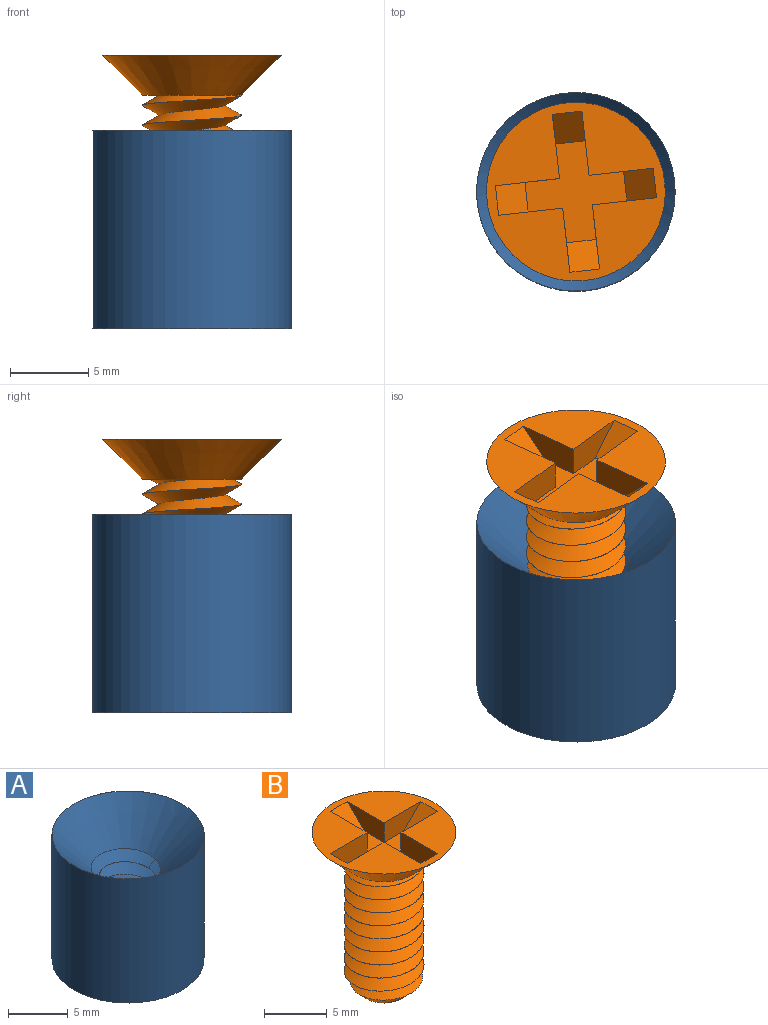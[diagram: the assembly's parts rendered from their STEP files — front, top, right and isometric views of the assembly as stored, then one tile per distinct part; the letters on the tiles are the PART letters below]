
ASSEMBLY  parts=2 mates=1
PART A: 9 faces, bbox 12.7x12.7x13.3 mm
  f0: plane 12.7x12.7mm, normal (0,0,-1), area 99.3mm2, adj f2,f5,f6
  f1: cylinder r=2.39mm len=8.74mm, axis (0,0,-1), area -8.6mm2, adj f5,f6,f8
  f2: cylinder r=6.35mm len=12.7mm, axis (0,0,-1), area 506.7mm2, adj f0,f3
  f3: plane 12.7x12.7mm, normal (0,0,1), area 0.1mm2, adj f2,f4
  f4: cone r=2.39mm half-angle=45deg, axis (0,0,1), area 140.3mm2, adj f3,f6,f7,f8
  f5: bspline ~9.37x6.97mm, area 155.6mm2, adj f0,f1,f6,f8
  f6: bspline ~10.01x6.97mm, area 166mm2, adj f0,f1,f4,f5,f7,f8
  f7: bspline ~8.05x6.97mm, area 7.1mm2, adj f4,f6,f8
  f8: bspline ~6.97x6.97mm, area 16.3mm2, adj f1,f4,f5,f6,f7
PART B: 22 faces, bbox 12.3x12.3x16.7 mm
  f0: cylinder r=3.17mm len=11.43mm, axis (0,0,-1), area 0mm2, adj f3,f4,f5,f7
  f1: plane 3.81x3.81mm, normal (0,0,-1), area 11.4mm2, adj f2
  f2: cone r=3.17mm half-angle=45deg, axis (0,0,1), area 15mm2, adj f1,f3,f4,f5
  f3: cone r=3.17mm half-angle=45deg, axis (0,0,1), area 0mm2, adj f0,f2,f5
  f4: bspline ~13.97x7.33mm, area 196.3mm2, adj f0,f2,f5,f6
  f5: bspline ~13.55x7.33mm, area 197.8mm2, adj f0,f2,f3,f4,f6
  f6: plane 7.22x7.22mm, normal (0,0,-1), area 9.7mm2, adj f4,f5,f7
  f7: cone r=3.17mm half-angle=45deg, axis (0,0,1), area 100.3mm2, adj f0,f6,f8
  f8: plane 11.43x11.43mm, normal (0,0,1), area 67.5mm2, adj f7,f9,f10,f11,f12,f13,f14,f15
  f9: plane 4.13x1.91mm, normal (0,-1,0), area 6mm2, adj f8,f10,f17,f20
  f10: plane 4.13x1.91mm, normal (-1,0,0), area 6mm2, adj f8,f9,f17,f21
  f11: plane 4.13x1.91mm, normal (1,0,0), area 6mm2, adj f8,f12,f17,f21
  f12: plane 4.13x1.91mm, normal (0,-1,0), area 6mm2, adj f8,f11,f17,f18
  f13: plane 4.13x1.91mm, normal (0,1,0), area 6mm2, adj f8,f14,f17,f18
  f14: plane 4.13x1.91mm, normal (1,0,0), area 6mm2, adj f8,f13,f17,f19
  f15: plane 4.13x1.91mm, normal (-1,0,0), area 6mm2, adj f8,f16,f17,f19
  f16: plane 4.13x1.91mm, normal (0,1,0), area 6mm2, adj f8,f15,f17,f20
  f17: plane 6.35x6.35mm, normal (0,0,1), area 20.6mm2, adj f9,f10,f11,f12,f13,f14,f15,f16
  f18: plane 1.91x1.91mm, normal (0.71,0,0.71), area 5.1mm2, adj f8,f12,f13,f17
  f19: plane 1.91x1.91mm, normal (0,0.71,0.71), area 5.1mm2, adj f8,f14,f15,f17
  f20: plane 1.91x1.91mm, normal (-0.71,0,0.71), area 5.1mm2, adj f8,f9,f16,f17
  f21: plane 1.91x1.91mm, normal (0,-0.71,0.71), area 5.1mm2, adj f8,f10,f11,f17
PLACE A t=(-22.27,5.08,-4.54)mm fixed
PLACE B rot(axis=(0,0,1),6.3deg) t=(6.7,5.08,-2.29)mm
MATE cylindrical A.f1 <-> B.f0  axis (0,0,-1) through (6.7,5.08,-4.54)mm
